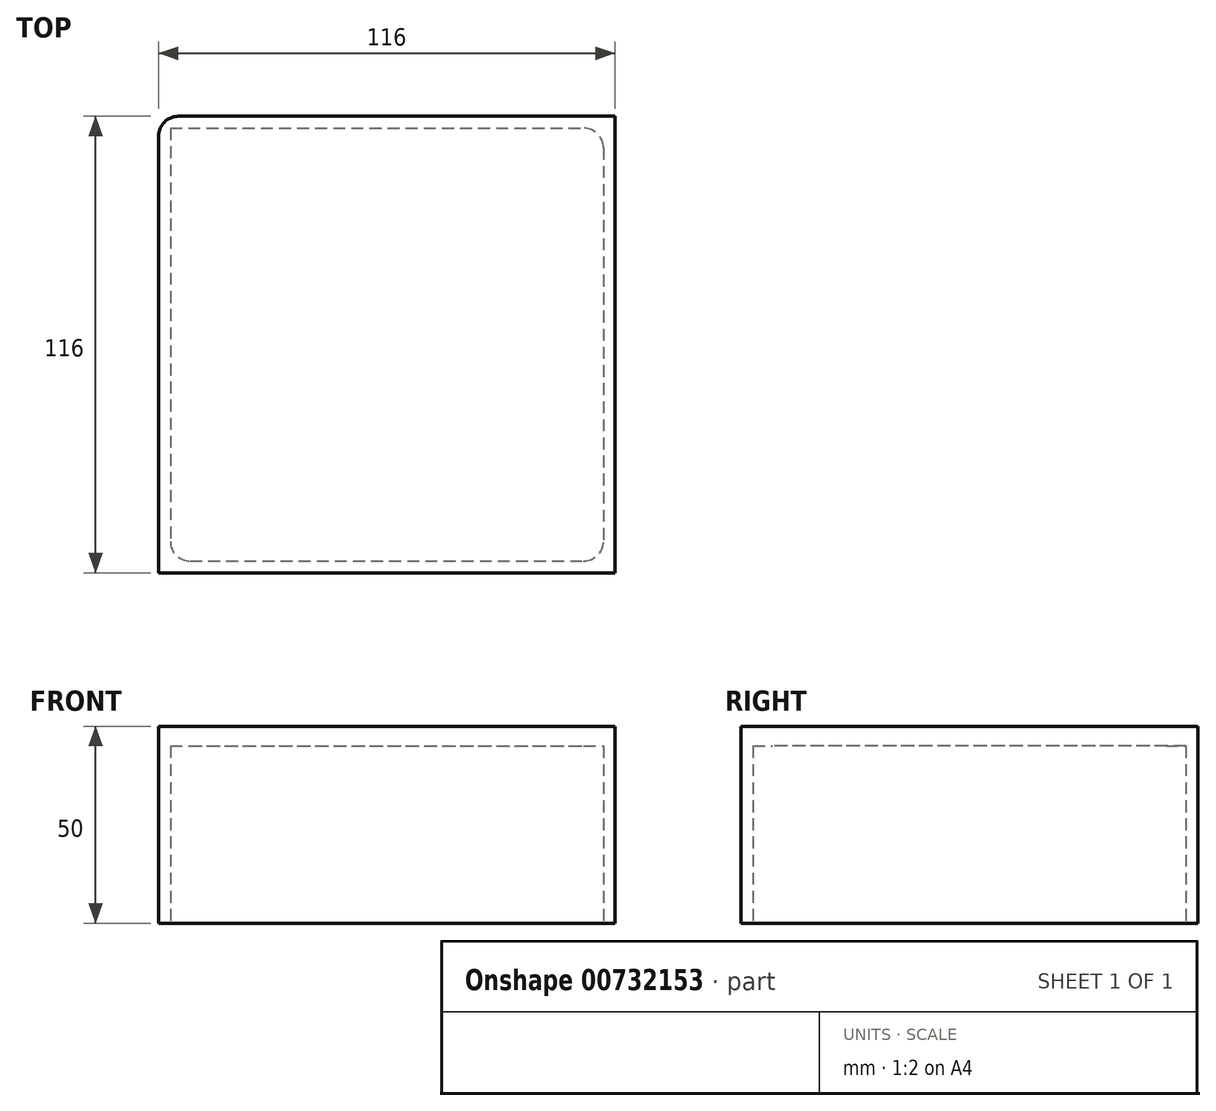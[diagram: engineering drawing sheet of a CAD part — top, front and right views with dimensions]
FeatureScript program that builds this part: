
annotation { "Feature Type Name" : "Feature", "Feature Type Description" : "" }
export const myFeature = defineFeature(function(context is Context, id is Id, definition is map)
    precondition{}
    {
        {
            var Q0;
            Q0=qCreatedBy(makeId("Top.planeOp"),FACE);
            var sketch = newSketch(context, id + "F0", { "sketchPlane" : qUnion([Q0])});
            skLineSegment(sketch, "E0.bottom", {"start": v(-58, 58) * mm, "end": v(58, 58) * mm});
            skLineSegment(sketch, "E0.top", {"start": v(-58, -58) * mm, "end": v(58, -58) * mm});
            skLineSegment(sketch, "E0.left", {"start": v(-58, 58) * mm, "end": v(-58, -58) * mm});
            skLineSegment(sketch, "E0.right", {"start": v(58, 58) * mm, "end": v(58, -58) * mm});
            skPoint(sketch, "E0.middle", {"position": v(0, 0) * mm});
            skSolve(sketch);
        }
        {
            var Q0;
            Q0=qSketchRegion(id+"F0",true);
            extrude(context, id + "F1", {"entities" : qUnion([Q0]), "depth" : 50 * mm, "offsetDistance" : 25 * mm});
        }
        {
            var Q0;
            Q0=qCreatedBy(makeId("Top.planeOp"),FACE);
            var sketch = newSketch(context, id + "F2", { "sketchPlane" : qUnion([Q0])});
            skLineSegment(sketch, "E1.bottom", {"start": v(-55, 55) * mm, "end": v(55, 55) * mm});
            skLineSegment(sketch, "E1.top", {"start": v(-55, -55) * mm, "end": v(55, -55) * mm});
            skLineSegment(sketch, "E1.left", {"start": v(-55, 55) * mm, "end": v(-55, -55) * mm});
            skLineSegment(sketch, "E1.right", {"start": v(55, 55) * mm, "end": v(55, -55) * mm});
            skPoint(sketch, "E1.middle", {"position": v(0, 0) * mm});
            skSolve(sketch);
        }
        {
            var Q0;
            Q0=qSketchRegion(id+"F2",true);
            extrude(context, id + "F3", {"entities" : qUnion([Q0]), "operationType" : NewBodyOperationType.REMOVE, "depth" : 45 * mm, "offsetDistance" : 25 * mm});
        }
        {
            var Q0;
            Q0=makeQuery(id+"F1.opExtrude","SWEPT_EDGE",EDGE,{"disambiguationData":[OSD([sQuery(id+"F0.wireOp",EDGE,"E0.bottom"),sQuery(id+"F0.wireOp",EDGE,"E0.left")])]});
            var Q1;
            Q1=makeQuery(id+"F3.boolean.opBoolean","COPY",EDGE,{"derivedFrom":makeQuery(id+"F3.opExtrude","SWEPT_EDGE",EDGE,{"disambiguationData":[OSD([sQuery(id+"F2.wireOp",EDGE,"E1.bottom"),sQuery(id+"F2.wireOp",EDGE,"E1.right")])]})});
            var Q2;
            Q2=makeQuery(id+"F3.boolean.opBoolean","COPY",EDGE,{"derivedFrom":makeQuery(id+"F3.opExtrude","SWEPT_EDGE",EDGE,{"disambiguationData":[OSD([sQuery(id+"F2.wireOp",EDGE,"E1.top"),sQuery(id+"F2.wireOp",EDGE,"E1.left")])]})});
            var Q3;
            Q3=makeQuery(id+"F3.boolean.opBoolean","COPY",EDGE,{"derivedFrom":makeQuery(id+"F3.opExtrude","SWEPT_EDGE",EDGE,{"disambiguationData":[OSD([sQuery(id+"F2.wireOp",EDGE,"E1.top"),sQuery(id+"F2.wireOp",EDGE,"E1.right")])]})});
            fillet(context, id + "F4", {"entities" : qUnion([Q0, Q1, Q2, Q3]), "radius" : 5 * mm, "tangentPropagation" : true, "allowEdgeOverflow" : false});
        }
    });
